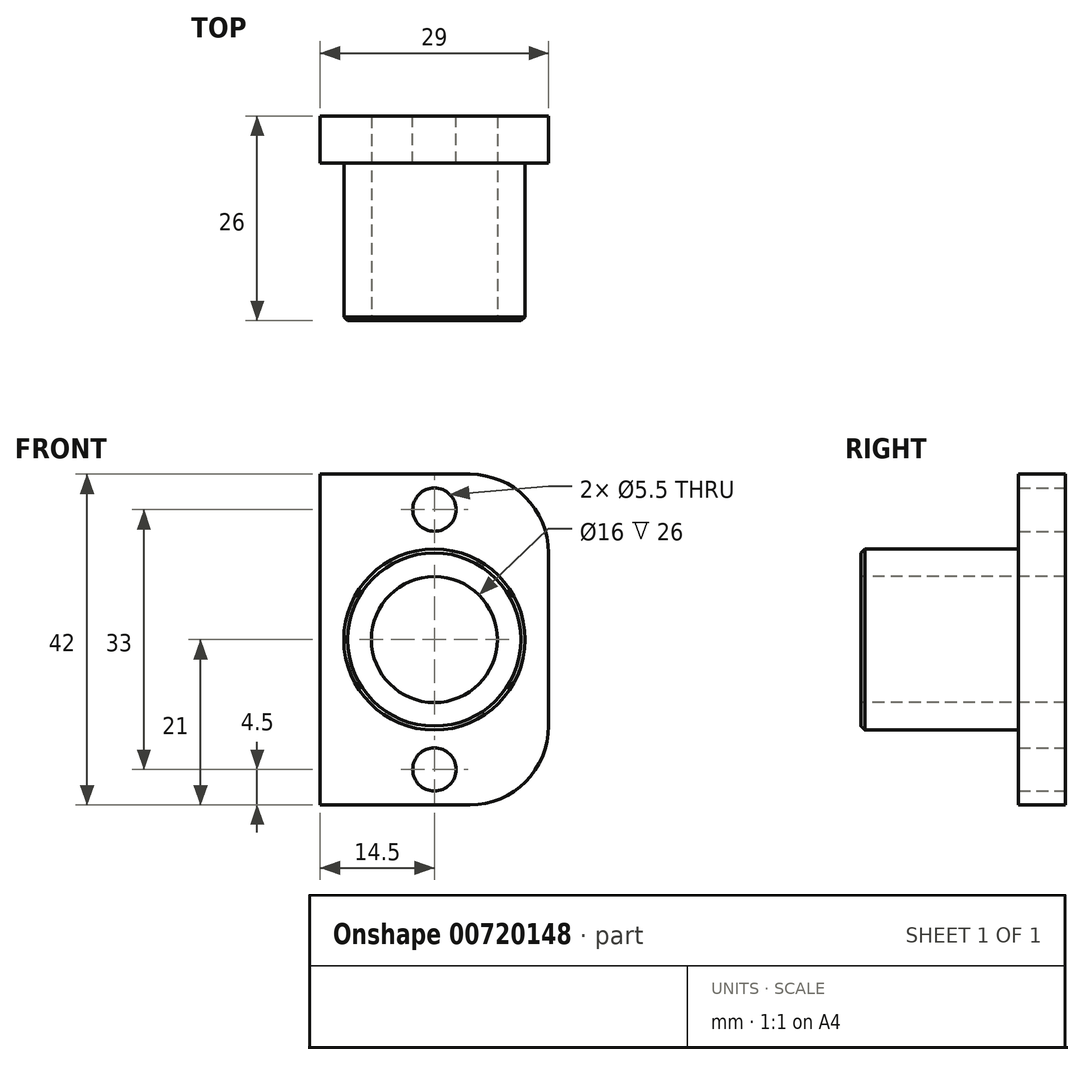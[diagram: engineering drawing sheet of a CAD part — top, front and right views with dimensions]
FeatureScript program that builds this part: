
annotation { "Feature Type Name" : "Feature", "Feature Type Description" : "" }
export const myFeature = defineFeature(function(context is Context, id is Id, definition is map)
    precondition{}
    {
        {
            var Q0;
            Q0=qCreatedBy(makeId("Front.planeOp"),FACE);
            var sketch = newSketch(context, id + "F0", { "sketchPlane" : qUnion([Q0])});
            skCircle(sketch, "E0", {"center": v(14.5, 37.5) * mm, "radius": 2.75 * mm});
            skCircle(sketch, "E1", {"center": v(14.5, 4.5) * mm, "radius": 2.75 * mm});
            skLineSegment(sketch, "E2.bottom", {"start": v(0, 0) * mm, "end": v(19, 0) * mm});
            skLineSegment(sketch, "E2.top", {"start": v(0, 42) * mm, "end": v(19, 42) * mm});
            skLineSegment(sketch, "E2.left", {"start": v(0, 0) * mm, "end": v(0, 42) * mm});
            skLineSegment(sketch, "E2.right", {"start": v(29, 10) * mm, "end": v(29, 32) * mm});
            skPoint(sketch, "E3.visualSharp", {"position": v(29, 42) * mm});
            skArc(sketch, "E3.filletArc", {"start": v(29, 32) * mm, "mid": v(26.07, 39.07) * mm, "end": v(19, 42) * mm});
            skPoint(sketch, "E4.visualSharp", {"position": v(29, 0) * mm});
            skArc(sketch, "E4.filletArc", {"start": v(19, 0) * mm, "mid": v(26.07, 2.93) * mm, "end": v(29, 10) * mm});
            skSolve(sketch);
        }
        {
            var Q0;
            Q0 = qSketchRegion(id + "F0", true);
            extrude(context, id + "F1", {"entities" : qUnion([Q0]), "depth" : 6 * mm, "offsetDistance" : 25 * mm});
        }
        {
            var Q0;
            Q0=makeQuery(id+"F1.opExtrude","CAP_FACE",FACE,{"disambiguationData":[OSD([sQuery(id+"F0.wireOp",EDGE,"GElbZ2Az-jKSd-r07h-xSZ2-ESVE7XzwhFKq.bottom"),sQuery(id+"F0.wireOp",EDGE,"GElbZ2Az-jKSd-r07h-xSZ2-ESVE7XzwhFKq.top"),sQuery(id+"F0.wireOp",EDGE,"GElbZ2Az-jKSd-r07h-xSZ2-ESVE7XzwhFKq.left"),sQuery(id+"F0.wireOp",EDGE,"GElbZ2Az-jKSd-r07h-xSZ2-ESVE7XzwhFKq.right"),sQuery(id+"F0.wireOp",EDGE,"lIkirdat-Yk2o-svgg-tQx5-F4zSsNhtWoR0"),sQuery(id+"F0.wireOp",EDGE,"4f5bbfff-1af3-4ae1-ae6d-97baef97d8b1.trimOffspring"),sQuery(id+"F0.wireOp",EDGE,"ef988cb2-40da-40f5-93de-d70cc30f40bf.trimOffspring"),sQuery(id+"F0.wireOp",EDGE,"ff232ffd-c0bb-4f31-99bc-5b63c790d028.trimOffspring"),sQuery(id+"F0.wireOp",EDGE,"E0"),sQuery(id+"F0.wireOp",EDGE,"E1")])],"isStart":false});
            var sketch = newSketch(context, id + "F2", { "sketchPlane" : qUnion([Q0])});
            skCircle(sketch, "E5", {"center": v(14.5, 21) * mm, "radius": 11.5 * mm});
            skSolve(sketch);
        }
        {
            var Q0;
            Q0=makeQuery(id+"F2.imprint","IMPRINT",FACE,{"disambiguationData":[TD([[makeQuery(id+"F2.imprint","IMPRINT",EDGE,{"derivedFrom":sQuery(id+"F2.wireOp",EDGE,"E5")}),1.0]])]});
            extrude(context, id + "F3", {"entities" : qUnion([Q0]), "operationType" : NewBodyOperationType.ADD, "depth" : 20 * mm, "offsetDistance" : 25 * mm});
        }
        {
            var Q0;
            Q0=makeQuery(id+"F3.opExtrude","CAP_FACE",FACE,{"disambiguationData":[OSD([sQuery(id+"F2.wireOp",EDGE,"E5")])],"isStart":false});
            var sketch = newSketch(context, id + "F4", { "sketchPlane" : qUnion([Q0])});
            skCircle(sketch, "E6", {"center": v(14.5, 21) * mm, "radius": 8 * mm});
            skSolve(sketch);
        }
        {
            var Q0;
            Q0=makeQuery(id+"F4.imprint","IMPRINT",FACE,{"disambiguationData":[TD([[makeQuery(id+"F4.imprint","IMPRINT",EDGE,{"derivedFrom":sQuery(id+"F4.wireOp",EDGE,"E6")}),1.0]])]});
            extrude(context, id + "F5", {"entities" : qUnion([Q0]), "operationType" : NewBodyOperationType.REMOVE, "endBound" : BoundingType.THROUGH_ALL, "oppositeDirection" : true, "depth" : 25 * mm, "offsetDistance" : 25 * mm});
        }
        {
            var Q0;
            Q0=makeQuery(id+"F3.opExtrude","CAP_EDGE",EDGE,{"disambiguationData":[OSD([sQuery(id+"F2.wireOp",EDGE,"E5")])],"isStart":false});
            chamfer(context, id + "F6", {"entities" : qUnion([Q0]), "width" : .5 * mm, "tangentPropagation" : true});
        }
    });
